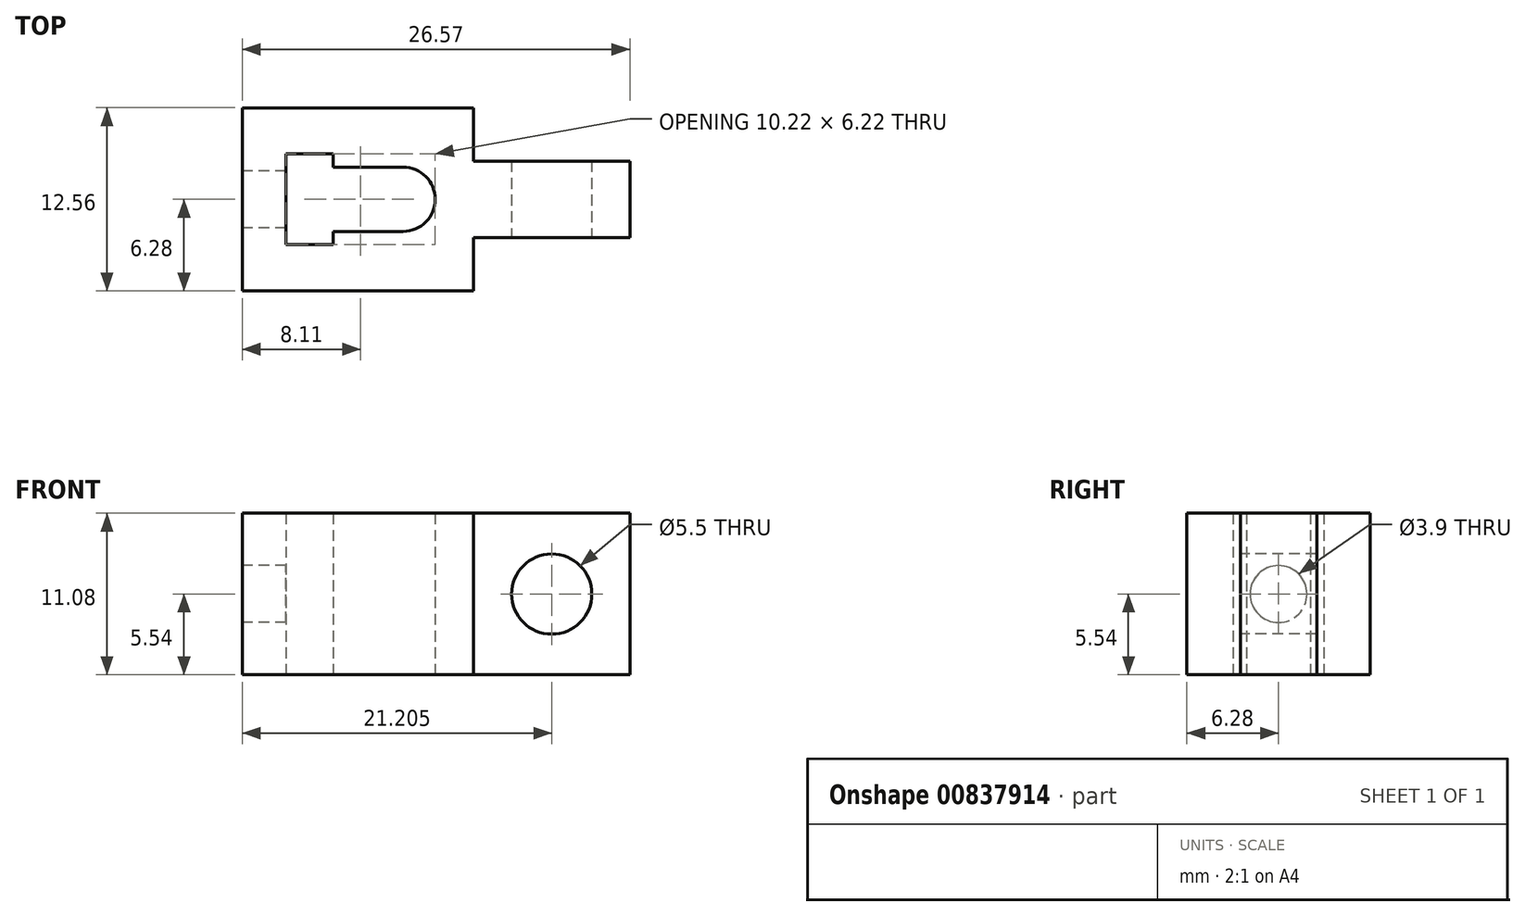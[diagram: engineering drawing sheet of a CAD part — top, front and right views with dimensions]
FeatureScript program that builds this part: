
annotation { "Feature Type Name" : "Feature", "Feature Type Description" : "" }
export const myFeature = defineFeature(function(context is Context, id is Id, definition is map)
    precondition{}
    {
        {
            var Q0;
            Q0=qCreatedBy(makeId("Top.planeOp"),FACE);
            var sketch = newSketch(context, id + "F0", { "sketchPlane" : qUnion([Q0])});
            skLineSegment(sketch, "E0.bottom", {"start": v(-15.84, 6.28) * mm, "end": v(0, 6.28) * mm});
            skLineSegment(sketch, "E0.top", {"start": v(-15.84, -6.28) * mm, "end": v(0, -6.28) * mm});
            skLineSegment(sketch, "E0.left", {"start": v(-15.84, 6.27) * mm, "end": v(-15.84, -6.27) * mm});
            skLineSegment(sketch, "E0.right", {"start": v(0, 6.28) * mm, "end": v(0, -6.28) * mm});
            skLineSegment(sketch, "E1.bottom", {"start": v(0, 2.62) * mm, "end": v(10.73, 2.62) * mm});
            skLineSegment(sketch, "E1.top", {"start": v(0, -2.62) * mm, "end": v(10.73, -2.62) * mm});
            skLineSegment(sketch, "E1.left", {"start": v(0, 2.62) * mm, "end": v(0, -2.62) * mm});
            skLineSegment(sketch, "E1.right", {"start": v(10.73, 2.62) * mm, "end": v(10.73, -2.62) * mm});
            skLineSegment(sketch, "E2.bottom", {"start": v(-12.84, 3.1) * mm, "end": v(-9.62, 3.1) * mm});
            skLineSegment(sketch, "E2.top", {"start": v(-12.84, -3.11) * mm, "end": v(-9.62, -3.11) * mm});
            skLineSegment(sketch, "E2.left", {"start": v(-12.84, 3.1) * mm, "end": v(-12.84, -3.11) * mm});
            skLineSegment(sketch, "E2.right", {"start": v(-9.62, 3.1) * mm, "end": v(-9.62, -3.11) * mm});
            skPoint(sketch, "E3", {"position": v(-12.84, 0) * mm});
            skLineSegment(sketch, "E4.bottom", {"start": v(-9.62, 2.2) * mm, "end": v(-4.82, 2.2) * mm});
            skLineSegment(sketch, "E4.top", {"start": v(-9.62, -2.2) * mm, "end": v(-4.82, -2.2) * mm});
            skLineSegment(sketch, "E4.left", {"start": v(-9.62, 2.2) * mm, "end": v(-9.62, -2.2) * mm});
            skLineSegment(sketch, "E4.right", {"start": v(-4.82, 2.2) * mm, "end": v(-4.82, -2.2) * mm});
            skPoint(sketch, "E5", {"position": v(-4.82, 0) * mm});
            skCircle(sketch, "E6", {"center": v(-4.82, 0) * mm, "radius": 2.2 * mm});
            skSolve(sketch);
        }
        {
            var Q0;
            Q0 = qSketchRegion(id + "F0", true);
            extrude(context, id + "F1", {"entities" : qUnion([Q0]), "depth" : 11.08 * mm, "offsetDistance" : 25 * mm});
        }
        {
            var Q0;
            Q0=makeQuery(id+"F1.opExtrude","SWEPT_FACE",FACE,{"disambiguationData":[OSD([sQuery(id+"F0.wireOp",EDGE,"E0.left")])]});
            var sketch = newSketch(context, id + "F2", { "sketchPlane" : qUnion([Q0])});
            skPoint(sketch, "E7", {"position": v(0, 5.54) * mm});
            skPoint(sketch, "E8", {"position": v(-6.27, 5.54) * mm});
            skSolve(sketch);
        }
        {
            var Q0;
            Q0=sQuery(id+"F2.wireOp",VERTEX,"E7");
            var Q1;
            Q1=makeQuery(id+"F1.opExtrude","SWEPT_BODY",BODY,{"disambiguationData":[OSD([sQuery(id+"F0.wireOp",EDGE,"E0.bottom"),sQuery(id+"F0.wireOp",EDGE,"E0.top"),sQuery(id+"F0.wireOp",EDGE,"E0.left"),sQuery(id+"F0.wireOp",EDGE,"E0.right"),sQuery(id+"F0.wireOp",EDGE,"E1.bottom"),sQuery(id+"F0.wireOp",EDGE,"E1.top"),sQuery(id+"F0.wireOp",EDGE,"E1.right"),sQuery(id+"F0.wireOp",EDGE,"E2.bottom"),sQuery(id+"F0.wireOp",EDGE,"E2.top"),sQuery(id+"F0.wireOp",EDGE,"E2.left"),sQuery(id+"F0.wireOp",EDGE,"E2.right"),sQuery(id+"F0.wireOp",EDGE,"E4.bottom"),sQuery(id+"F0.wireOp",EDGE,"E4.top"),sQuery(id+"F0.wireOp",EDGE,"E6")])]});
            hole(context, id + "F3", {"style" : HoleStyle.SIMPLE, "endStyle" : HoleEndStyle.BLIND, "holeDiameter" : 3.9 * mm, "majorDiameter" : 5 * mm, "holeDepth" : 12 * mm, "isTappedThrough" : true, "tappedDepth" : 12 * mm, "tapClearance" : 3, "locations" : qUnion([Q0]), "scope" : qUnion([Q1])});
        }
        {
            var Q0;
            Q0=makeQuery(id+"F1.opExtrude","SWEPT_FACE",FACE,{"disambiguationData":[OSD([sQuery(id+"F0.wireOp",EDGE,"E1.top")])]});
            var sketch = newSketch(context, id + "F4", { "sketchPlane" : qUnion([Q0])});
            skPoint(sketch, "E9", {"position": v(5.36, 5.54) * mm});
            skPoint(sketch, "E10", {"position": v(5.37, 11.08) * mm});
            skPoint(sketch, "E11", {"position": v(10.73, 5.54) * mm});
            skSolve(sketch);
        }
        {
            var Q0;
            Q0=sQuery(id+"F4.wireOp",VERTEX,"E9");
            var Q1;
            Q1=makeQuery(id+"F1.opExtrude","SWEPT_BODY",BODY,{"disambiguationData":[OSD([sQuery(id+"F0.wireOp",EDGE,"E0.bottom"),sQuery(id+"F0.wireOp",EDGE,"E0.top"),sQuery(id+"F0.wireOp",EDGE,"E0.left"),sQuery(id+"F0.wireOp",EDGE,"E0.right"),sQuery(id+"F0.wireOp",EDGE,"E1.bottom"),sQuery(id+"F0.wireOp",EDGE,"E1.top"),sQuery(id+"F0.wireOp",EDGE,"E1.right"),sQuery(id+"F0.wireOp",EDGE,"E2.bottom"),sQuery(id+"F0.wireOp",EDGE,"E2.top"),sQuery(id+"F0.wireOp",EDGE,"E2.left"),sQuery(id+"F0.wireOp",EDGE,"E2.right"),sQuery(id+"F0.wireOp",EDGE,"E4.bottom"),sQuery(id+"F0.wireOp",EDGE,"E4.top"),sQuery(id+"F0.wireOp",EDGE,"E6")])]});
            hole(context, id + "F5", {"style" : HoleStyle.SIMPLE, "endStyle" : HoleEndStyle.THROUGH, "holeDiameter" : 5.5 * mm, "majorDiameter" : 5 * mm, "isTappedThrough" : true, "tappedDepth" : 12 * mm, "tapClearance" : 3, "locations" : qUnion([Q0]), "scope" : qUnion([Q1])});
        }
    });
